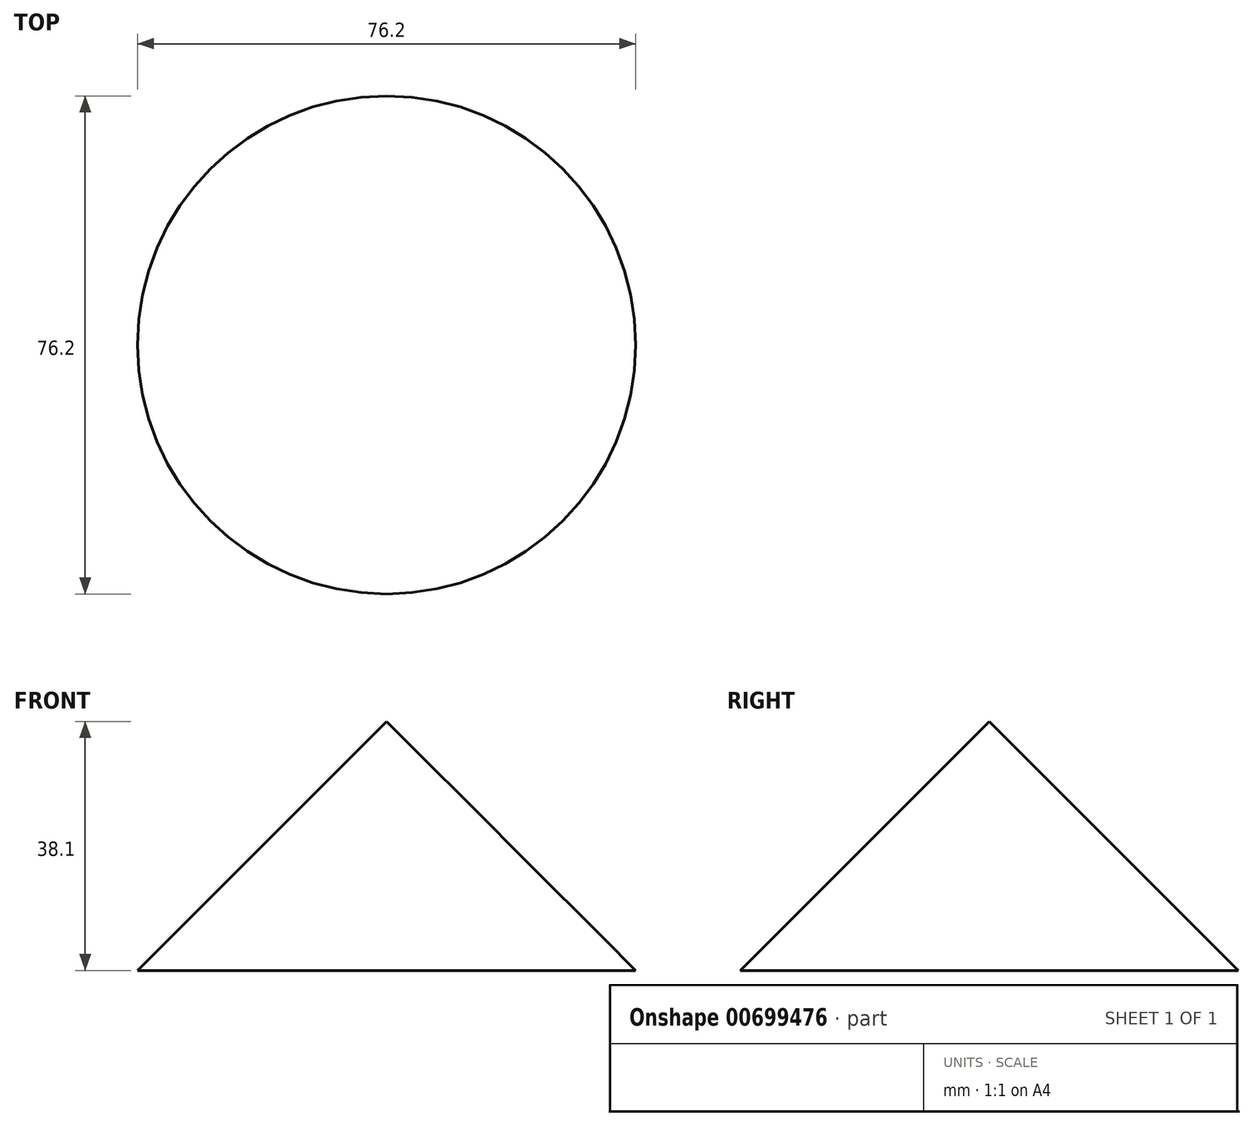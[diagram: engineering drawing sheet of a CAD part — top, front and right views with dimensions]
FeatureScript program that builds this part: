
annotation { "Feature Type Name" : "Feature", "Feature Type Description" : "" }
export const myFeature = defineFeature(function(context is Context, id is Id, definition is map)
    precondition{}
    {
        {
            var Q0;
            Q0=qCreatedBy(makeId("Top.planeOp"),FACE);
            var sketch = newSketch(context, id + "F0", { "sketchPlane" : qUnion([Q0])});
            skCircle(sketch, "E0", {"center": v(0, 0) * mm, "radius": 38.1 * mm});
            skSolve(sketch);
        }
        {
            var Q0;
            Q0 = qSketchRegion(id + "F0", true);
            extrude(context, id + "F1", {"entities" : qUnion([Q0]), "depth" : 76.2 * mm, "offsetDistance" : 25.4 * mm, "hasDraft" : true, "draftAngle" : 45 * degree, "draftPullDirection" : true});
        }
    });
